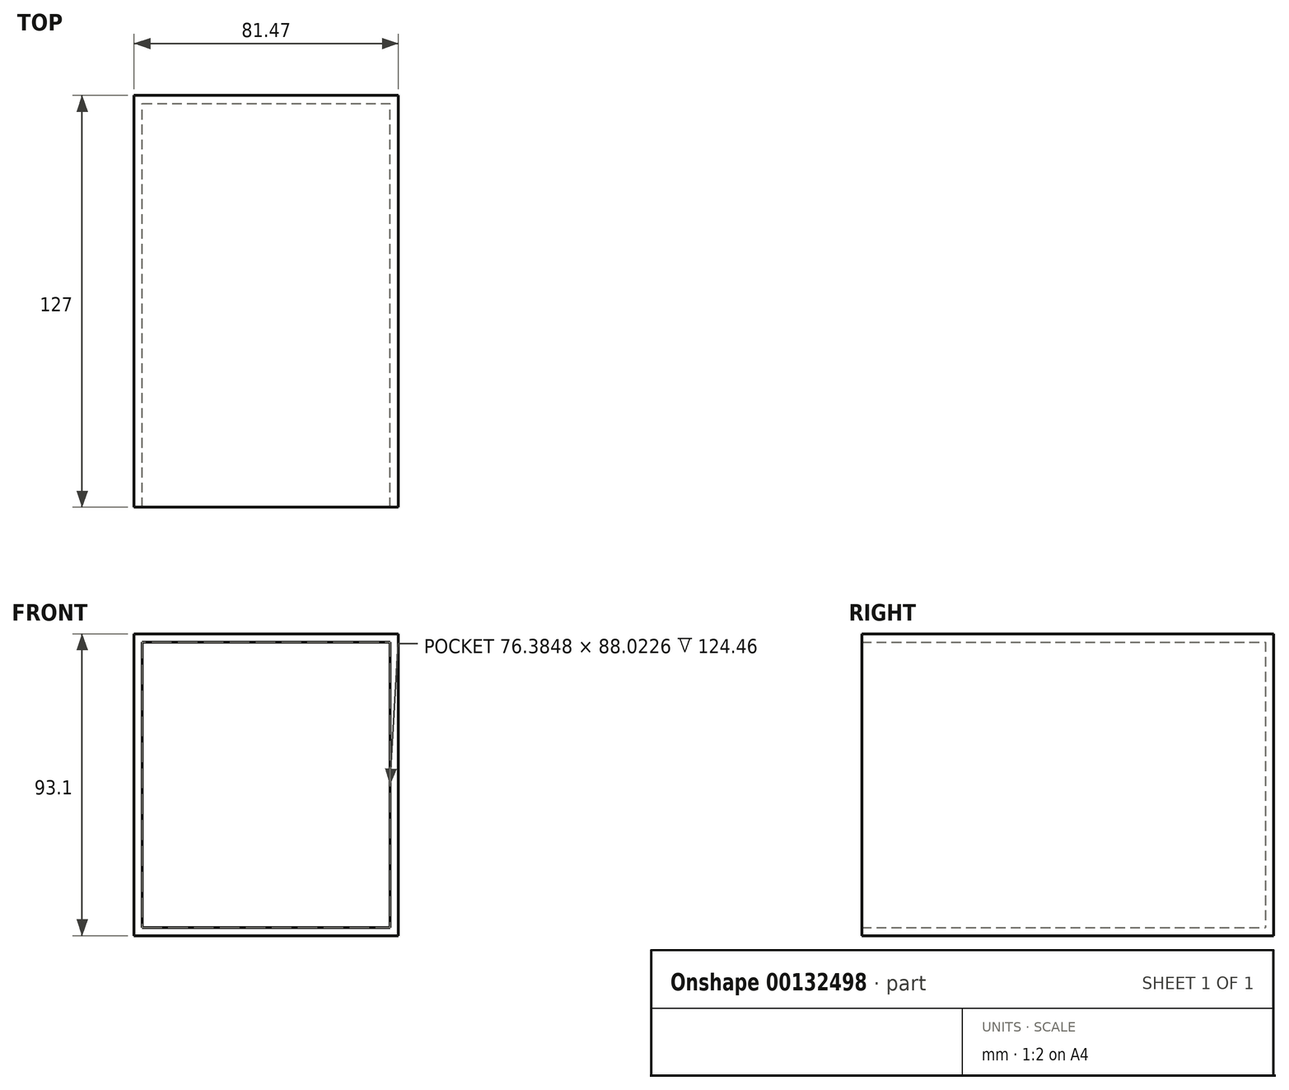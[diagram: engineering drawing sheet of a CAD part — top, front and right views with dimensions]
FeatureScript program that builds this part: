
annotation { "Feature Type Name" : "Feature", "Feature Type Description" : "" }
export const myFeature = defineFeature(function(context is Context, id is Id, definition is map)
    precondition{}
    {
        {
            var Q0;
            Q0=qCreatedBy(makeId("Front.planeOp"),FACE);
            var sketch = newSketch(context, id + "F0", { "sketchPlane" : qUnion([Q0])});
            skLineSegment(sketch, "E0.bottom", {"start": v(-42.07, 39.9) * mm, "end": v(39.4, 39.9) * mm});
            skLineSegment(sketch, "E0.top", {"start": v(-42.07, -53.2) * mm, "end": v(39.4, -53.2) * mm});
            skLineSegment(sketch, "E0.left", {"start": v(-42.07, 39.9) * mm, "end": v(-42.07, -53.2) * mm});
            skLineSegment(sketch, "E0.right", {"start": v(39.4, 39.9) * mm, "end": v(39.4, -53.2) * mm});
            skSolve(sketch);
        }
        {
            var Q0;
            Q0 = qSketchRegion(id + "F0", true);
            extrude(context, id + "F1", {"entities" : qUnion([Q0]), "depth" : 127 * mm});
        }
        {
            var Q0;
            Q0=makeQuery(id+"F1.opExtrude","CAP_FACE",FACE,{"disambiguationData":[OSD([sQuery(id+"F0.wireOp",EDGE,"E0.bottom"),sQuery(id+"F0.wireOp",EDGE,"E0.top"),sQuery(id+"F0.wireOp",EDGE,"E0.left"),sQuery(id+"F0.wireOp",EDGE,"E0.right")])],"isStart":false});
            shell(context, id + "F2", {"entities" : qUnion([Q0]), "thickness" : 2.54 * mm});
        }
    });
